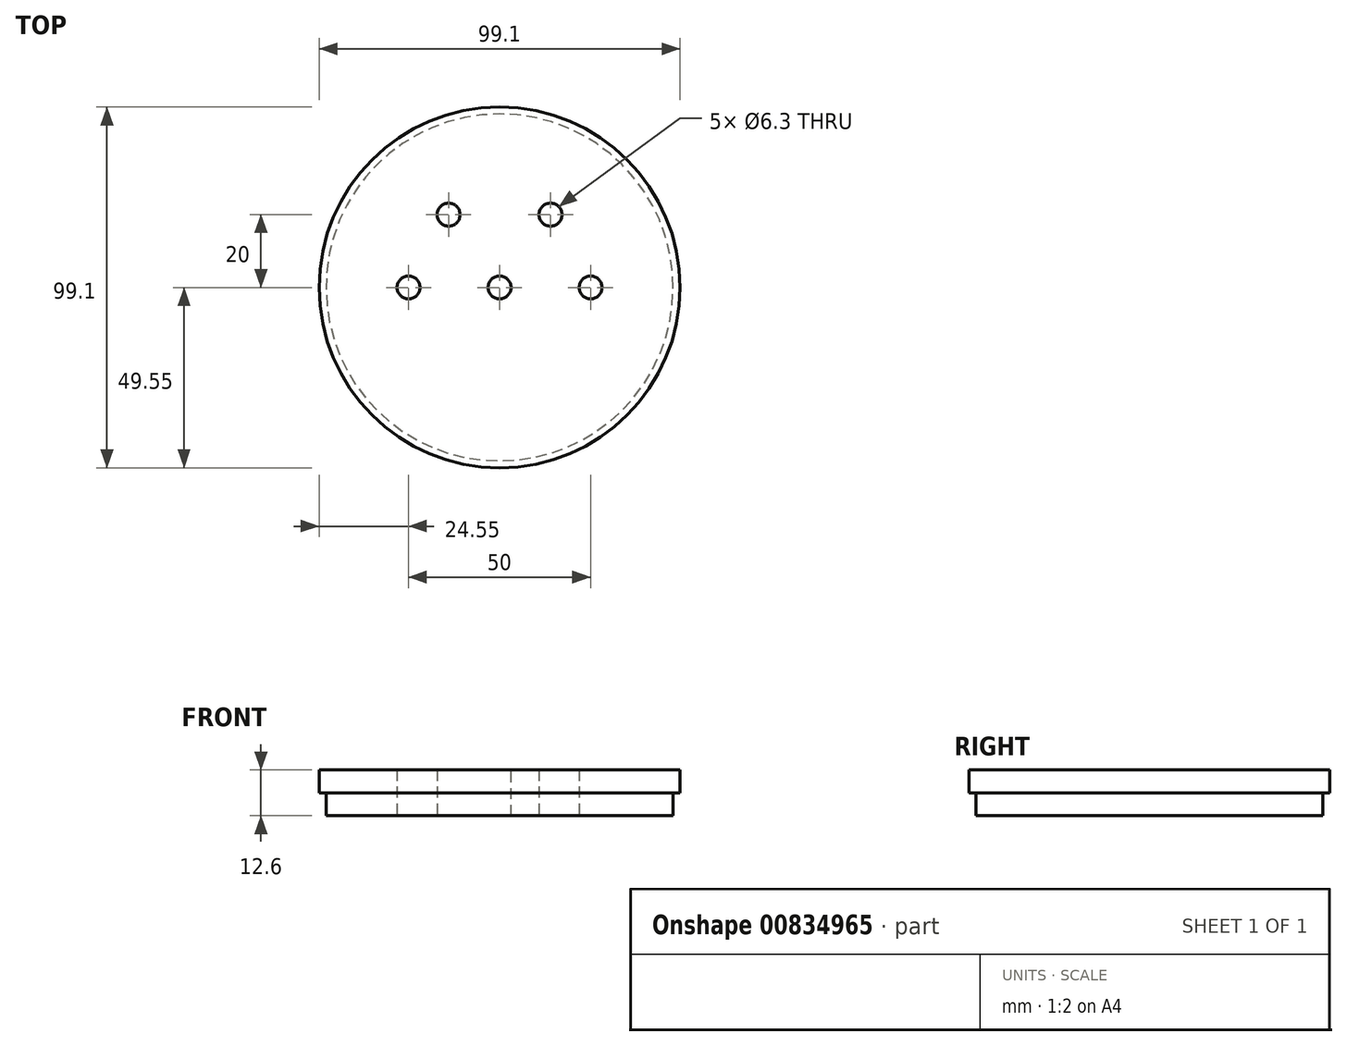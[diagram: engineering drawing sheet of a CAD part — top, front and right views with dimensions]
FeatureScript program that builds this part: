
annotation { "Feature Type Name" : "Feature", "Feature Type Description" : "" }
export const myFeature = defineFeature(function(context is Context, id is Id, definition is map)
    precondition{}
    {
        {
            var Q0;
            Q0=qCreatedBy(makeId("Front.planeOp"),FACE);
            var sketch = newSketch(context, id + "F0", { "sketchPlane" : qUnion([Q0])});
            skLineSegment(sketch, "E0", {"start": v(-47.65, 0) * mm, "end": v(-47.65, 6.3) * mm});
            skLineSegment(sketch, "E1", {"start": v(-47.65, 6.3) * mm, "end": v(-49.55, 6.3) * mm});
            skLineSegment(sketch, "E2", {"start": v(-49.55, 6.3) * mm, "end": v(-49.55, 12.6) * mm});
            skLineSegment(sketch, "E3", {"start": v(-49.55, 12.6) * mm, "end": v(-3.15, 12.6) * mm});
            skLineSegment(sketch, "E4", {"start": v(-3.15, 12.6) * mm, "end": v(-3.15, 0) * mm});
            skLineSegment(sketch, "E5", {"start": v(-3.15, 0) * mm, "end": v(-47.65, 0) * mm});
            skLineSegment(sketch, "E6", {"start": v(0, 2.5) * mm, "end": v(0, -12.8) * mm});
            skSolve(sketch);
        }
        {
            var Q0;
            Q0=makeQuery(id+"F0.imprint","IMPRINT",FACE,{"disambiguationData":[TD([[makeQuery(id+"F0.imprint","IMPRINT",EDGE,{"derivedFrom":sQuery(id+"F0.wireOp",EDGE,"E0")}),-1.0]])]});
            var Q1;
            Q1=sQuery(id+"F0.wireOp",EDGE,"E6");
            revolve(context, id + "F1", {"surfaceOperationType" : NewSurfaceOperationType.NEW, "entities" : qUnion([Q0]), "axis" : qUnion([Q1]), "revolveType" : RevolveType.FULL});
        }
        {
            var Q0;
            Q0=qCreatedBy(makeId("Top.planeOp"),FACE);
            var sketch = newSketch(context, id + "F2", { "sketchPlane" : qUnion([Q0])});
            skPoint(sketch, "E7", {"position": v(25, 0) * mm});
            skPoint(sketch, "E8", {"position": v(-25, 0) * mm});
            skSolve(sketch);
        }
        {
            var Q0;
            Q0=sQuery(id+"F2.wireOp",VERTEX,"E7");
            var Q1;
            Q1=sQuery(id+"F2.wireOp",VERTEX,"E8");
            var Q2;
            Q2=makeQuery(id+"F1.opRevolve","SWEPT_BODY",BODY,{"disambiguationData":[OSD([sQuery(id+"F0.wireOp",EDGE,"E0"),sQuery(id+"F0.wireOp",EDGE,"E1"),sQuery(id+"F0.wireOp",EDGE,"E2"),sQuery(id+"F0.wireOp",EDGE,"E3"),sQuery(id+"F0.wireOp",EDGE,"E4"),sQuery(id+"F0.wireOp",EDGE,"E5")])]});
            hole(context, id + "F3", {"style" : HoleStyle.SIMPLE, "endStyle" : HoleEndStyle.THROUGH, "oppositeDirection" : true, "holeDiameter" : 6.3 * mm, "majorDiameter" : 5 * mm, "isTappedThrough" : true, "tappedDepth" : 12 * mm, "tapClearance" : 3, "startFromSketch" : true, "locations" : qUnion([Q0, Q1]), "scope" : qUnion([Q2])});
        }
        {
            var Q0;
            Q0=qCreatedBy(makeId("Top.planeOp"),FACE);
            var sketch = newSketch(context, id + "F4", { "sketchPlane" : qUnion([Q0])});
            skPoint(sketch, "E9", {"position": v(14, 20) * mm});
            skPoint(sketch, "E10", {"position": v(-14, 20) * mm});
            skSolve(sketch);
        }
        {
            var Q0;
            Q0=sQuery(id+"F4.wireOp",VERTEX,"E10");
            var Q1;
            Q1=sQuery(id+"F4.wireOp",VERTEX,"E9");
            var Q2;
            Q2=makeQuery(id+"F1.opRevolve","SWEPT_BODY",BODY,{"disambiguationData":[OSD([sQuery(id+"F0.wireOp",EDGE,"E0"),sQuery(id+"F0.wireOp",EDGE,"E1"),sQuery(id+"F0.wireOp",EDGE,"E2"),sQuery(id+"F0.wireOp",EDGE,"E3"),sQuery(id+"F0.wireOp",EDGE,"E4"),sQuery(id+"F0.wireOp",EDGE,"E5")])]});
            hole(context, id + "F5", {"style" : HoleStyle.SIMPLE, "endStyle" : HoleEndStyle.THROUGH, "oppositeDirection" : true, "holeDiameter" : 6.3 * mm, "majorDiameter" : 5 * mm, "isTappedThrough" : true, "tappedDepth" : 12 * mm, "tapClearance" : 3, "startFromSketch" : true, "locations" : qUnion([Q0, Q1]), "scope" : qUnion([Q2])});
        }
    });
